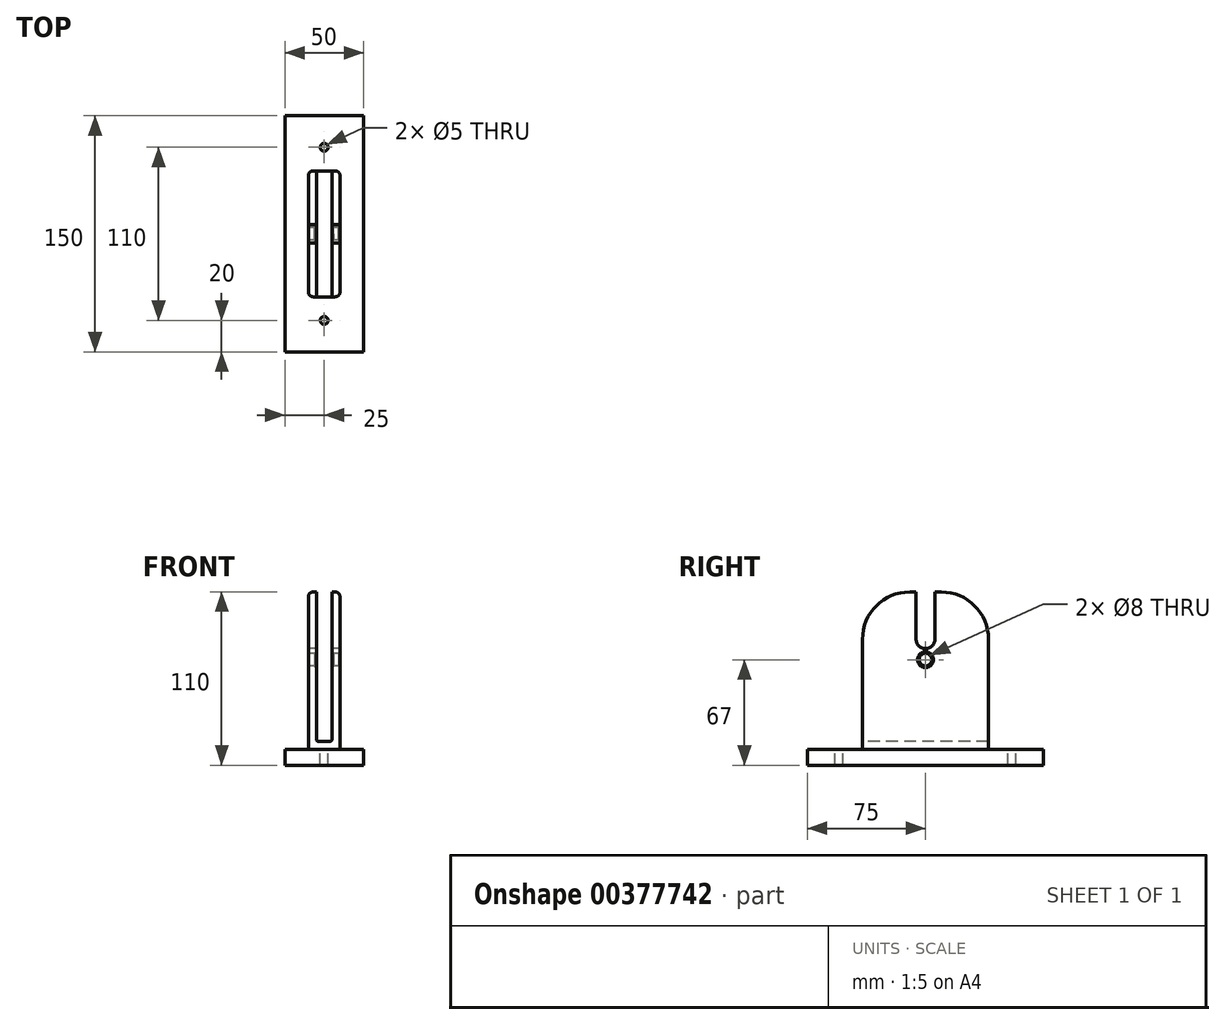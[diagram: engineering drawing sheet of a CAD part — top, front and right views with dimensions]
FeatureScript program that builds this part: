
annotation { "Feature Type Name" : "Feature", "Feature Type Description" : "" }
export const myFeature = defineFeature(function(context is Context, id is Id, definition is map)
    precondition{}
    {
        {
            var Q0;
            Q0=qCreatedBy(makeId("Top.planeOp"),FACE);
            var sketch = newSketch(context, id + "F0", { "sketchPlane" : qUnion([Q0])});
            skLineSegment(sketch, "E0.bottom", {"start": v(25, -75) * mm, "end": v(-25, -75) * mm});
            skLineSegment(sketch, "E0.top", {"start": v(25, 75) * mm, "end": v(-25, 75) * mm});
            skLineSegment(sketch, "E0.left", {"start": v(25, -75) * mm, "end": v(25, 75) * mm});
            skLineSegment(sketch, "E0.right", {"start": v(-25, -75) * mm, "end": v(-25, 75) * mm});
            skPoint(sketch, "E0.middle", {"position": v(0, 0) * mm});
            skLineSegment(sketch, "E1", {"start": v(0, 55) * mm, "end": v(0, -55) * mm, "construction": true});
            skCircle(sketch, "E2", {"center": v(0, 55) * mm, "radius": 2.5 * mm});
            skLineSegment(sketch, "E3", {"start": v(-25, 0) * mm, "end": v(25, 0) * mm, "construction": true});
            skCircle(sketch, "E4.MirrorC", {"center": v(0, -55) * mm, "radius": 2.5 * mm});
            skLineSegment(sketch, "E5.bottom", {"start": v(10, -40) * mm, "end": v(-10, -40) * mm});
            skLineSegment(sketch, "E5.top", {"start": v(10, 40) * mm, "end": v(-10, 40) * mm});
            skLineSegment(sketch, "E5.left", {"start": v(10, -40) * mm, "end": v(10, 40) * mm});
            skLineSegment(sketch, "E5.right", {"start": v(-10, -40) * mm, "end": v(-10, 40) * mm});
            skSolve(sketch);
        }
        {
            var Q0;
            Q0=makeQuery(id+"F0.imprint","IMPRINT",FACE,{"disambiguationData":[TD([[makeQuery(id+"F0.imprint","IMPRINT",EDGE,{"derivedFrom":sQuery(id+"F0.wireOp",EDGE,"E0.bottom")}),-1.0]])]});
            var Q1;
            Q1=makeQuery(id+"F0.imprint","IMPRINT",FACE,{"disambiguationData":[TD([[makeQuery(id+"F0.imprint","IMPRINT",EDGE,{"derivedFrom":sQuery(id+"F0.wireOp",EDGE,"E5.bottom")}),-1.0]])]});
            extrude(context, id + "F1", {"entities" : qUnion([Q0, Q1]), "oppositeDirection" : true, "depth" : 10 * mm});
        }
        {
            var Q0;
            Q0=makeQuery(id+"F0.imprint","IMPRINT",FACE,{"disambiguationData":[TD([[makeQuery(id+"F0.imprint","IMPRINT",EDGE,{"derivedFrom":sQuery(id+"F0.wireOp",EDGE,"E5.bottom")}),-1.0]])]});
            extrude(context, id + "F2", {"entities" : qUnion([Q0]), "operationType" : NewBodyOperationType.ADD, "depth" : 100 * mm});
        }
        {
            var Q0;
            Q0=makeQuery(id+"F2.opExtrude","SWEPT_FACE",FACE,{"disambiguationData":[OSD([sQuery(id+"F0.wireOp",EDGE,"E5.right")])]});
            var sketch = newSketch(context, id + "F3", { "sketchPlane" : qUnion([Q0])});
            skLineSegment(sketch, "E6", {"start": v(0, 100) * mm, "end": v(0, 0) * mm, "construction": true});
            skLineSegment(sketch, "E7", {"start": v(-40, 50) * mm, "end": v(40, 50) * mm, "construction": true});
            skLineSegment(sketch, "E8", {"start": v(-6, 100) * mm, "end": v(-6, 0) * mm, "construction": true});
            skLineSegment(sketch, "E9.MirrorCS", {"start": v(6, 100) * mm, "end": v(6, 0) * mm, "construction": true});
            skLineSegment(sketch, "E10", {"start": v(-40, 70) * mm, "end": v(40, 70) * mm, "construction": true});
            skLineSegment(sketch, "E11", {"start": v(-6, 70) * mm, "end": v(-6, 100) * mm});
            skLineSegment(sketch, "E12", {"start": v(6, 70) * mm, "end": v(6, 100) * mm});
            skArc(sketch, "E13", {"start": v(-6, 70) * mm, "mid": v(0, 64) * mm, "end": v(6, 70) * mm});
            skSolve(sketch);
        }
        {
            var Q0;
            {var subQ0=sQuery(id+"F3.wireOp",EDGE,"E11");Q0=makeQuery(id+"F3.imprint","IMPRINT",FACE,{"disambiguationData":[TD([[makeQuery(id+"F3.imprint","IMPRINT",EDGE,{"derivedFrom":subQ0}),-1.0]])]});}
            extrude(context, id + "F4", {"entities" : qUnion([Q0]), "operationType" : NewBodyOperationType.REMOVE, "endBound" : BoundingType.UP_TO_NEXT, "oppositeDirection" : true, "depth" : 25 * mm});
        }
        {
            var Q0;
            Q0=makeQuery(id+"F2.opExtrude","SWEPT_FACE",FACE,{"disambiguationData":[OSD([sQuery(id+"F0.wireOp",EDGE,"E5.bottom")])]});
            var sketch = newSketch(context, id + "F5", { "sketchPlane" : qUnion([Q0])});
            skLineSegment(sketch, "E14", {"start": v(0, 100) * mm, "end": v(0, 0) * mm, "construction": true});
            skLineSegment(sketch, "E15", {"start": v(-10, 5) * mm, "end": v(10, 5) * mm, "construction": true});
            skLineSegment(sketch, "E16", {"start": v(-5, 100) * mm, "end": v(-5, 0) * mm, "construction": true});
            skLineSegment(sketch, "E17.MirrorCS", {"start": v(5, 100) * mm, "end": v(5, 0) * mm, "construction": true});
            skLineSegment(sketch, "E18", {"start": v(-5, 100) * mm, "end": v(-5, 5) * mm});
            skLineSegment(sketch, "E19", {"start": v(-5, 5) * mm, "end": v(5, 5) * mm});
            skLineSegment(sketch, "E20", {"start": v(5, 5) * mm, "end": v(5, 100) * mm});
            skSolve(sketch);
        }
        {
            var Q0;
            {var subQ0=sQuery(id+"F5.wireOp",EDGE,"E18");Q0=makeQuery(id+"F5.imprint","IMPRINT",FACE,{"disambiguationData":[TD([[makeQuery(id+"F5.imprint","IMPRINT",EDGE,{"derivedFrom":subQ0}),1.0]])]});}
            extrude(context, id + "F6", {"entities" : qUnion([Q0]), "operationType" : NewBodyOperationType.REMOVE, "endBound" : BoundingType.THROUGH_ALL, "oppositeDirection" : true, "depth" : 25 * mm});
        }
        {
            var Q0;
            {var subQ0=sQuery(id+"F5.wireOp",EDGE,"E19");var subQ1=sQuery(id+"F5.wireOp",EDGE,"E20");Q0=makeQuery(id+"F6.boolean.opBoolean","COPY",EDGE,{"disambiguationData":[TD([makeQuery(id+"F2.opExtrude","SWEPT_FACE",FACE,{"disambiguationData":[OSD([sQuery(id+"F0.wireOp",EDGE,"E5.top")])]})])],"derivedFrom":makeQuery(id+"F6.opExtrude","SWEPT_EDGE",EDGE,{"disambiguationData":[OSD([subQ0,subQ1])]})});}
            var Q1;
            {var subQ0=sQuery(id+"F5.wireOp",EDGE,"E19");var subQ1=sQuery(id+"F5.wireOp",EDGE,"E20");Q1=makeQuery(id+"F6.boolean.opBoolean","COPY",EDGE,{"disambiguationData":[TD([makeQuery(id+"F2.opExtrude","SWEPT_FACE",FACE,{"disambiguationData":[OSD([sQuery(id+"F0.wireOp",EDGE,"E5.bottom")])]})])],"derivedFrom":makeQuery(id+"F6.opExtrude","SWEPT_EDGE",EDGE,{"disambiguationData":[OSD([subQ0,subQ1])]})});}
            var Q2;
            {var subQ0=sQuery(id+"F5.wireOp",EDGE,"E18");var subQ1=sQuery(id+"F5.wireOp",EDGE,"E19");Q2=makeQuery(id+"F6.boolean.opBoolean","COPY",EDGE,{"disambiguationData":[TD([makeQuery(id+"F2.opExtrude","SWEPT_FACE",FACE,{"disambiguationData":[OSD([sQuery(id+"F0.wireOp",EDGE,"E5.top")])]})])],"derivedFrom":makeQuery(id+"F6.opExtrude","SWEPT_EDGE",EDGE,{"disambiguationData":[OSD([subQ0,subQ1])]})});}
            var Q3;
            {var subQ0=sQuery(id+"F5.wireOp",EDGE,"E18");var subQ1=sQuery(id+"F5.wireOp",EDGE,"E19");Q3=makeQuery(id+"F6.boolean.opBoolean","COPY",EDGE,{"disambiguationData":[TD([makeQuery(id+"F2.opExtrude","SWEPT_FACE",FACE,{"disambiguationData":[OSD([sQuery(id+"F0.wireOp",EDGE,"E5.bottom")])]})])],"derivedFrom":makeQuery(id+"F6.opExtrude","SWEPT_EDGE",EDGE,{"disambiguationData":[OSD([subQ0,subQ1])]})});}
            fillet(context, id + "F7", {"entities" : qUnion([Q0, Q1, Q2, Q3]), "radius" : 1.5 * mm, "tangentPropagation" : true, "allowEdgeOverflow" : false});
        }
        {
            var Q0;
            Q0=makeQuery(id+"F2.opExtrude","SWEPT_FACE",FACE,{"disambiguationData":[OSD([sQuery(id+"F0.wireOp",EDGE,"E5.right")])]});
            var sketch = newSketch(context, id + "F8", { "sketchPlane" : qUnion([Q0])});
            skLineSegment(sketch, "E21", {"start": v(0, 0) * mm, "end": v(0, 64) * mm, "construction": true});
            skLineSegment(sketch, "E22", {"start": v(-40, 57) * mm, "end": v(40, 57) * mm, "construction": true});
            skCircle(sketch, "E23", {"center": v(0, 57) * mm, "radius": 4 * mm});
            skSolve(sketch);
        }
        {
            var Q0;
            Q0=makeQuery(id+"F8.imprint","IMPRINT",FACE,{"disambiguationData":[TD([[makeQuery(id+"F8.imprint","IMPRINT",EDGE,{"derivedFrom":sQuery(id+"F8.wireOp",EDGE,"E23")}),1.0]])]});
            extrude(context, id + "F9", {"entities" : qUnion([Q0]), "operationType" : NewBodyOperationType.REMOVE, "endBound" : BoundingType.THROUGH_ALL, "oppositeDirection" : true, "depth" : 25 * mm});
        }
        {
            var Q0;
            Q0=makeQuery(id+"F9.boolean.opBoolean","COPY",EDGE,{"derivedFrom":makeQuery(id+"F9.opExtrude","CAP_EDGE",EDGE,{"disambiguationData":[OSD([sQuery(id+"F8.wireOp",EDGE,"E23")])],"isStart":true})});
            var Q1;
            Q1=makeQuery(id+"F9.boolean.opBoolean","INTERSECT",EDGE,{"derivedFrom":[makeQuery(id+"F6.boolean.opBoolean","COPY",FACE,{"derivedFrom":makeQuery(id+"F6.opExtrude","SWEPT_FACE",FACE,{"disambiguationData":[OSD([sQuery(id+"F5.wireOp",EDGE,"E18")])]})}),makeQuery(id+"F9.opExtrude","SWEPT_FACE",FACE,{"disambiguationData":[OSD([sQuery(id+"F8.wireOp",EDGE,"E23")])]})]});
            var Q2;
            Q2=makeQuery(id+"F9.boolean.opBoolean","INTERSECT",EDGE,{"derivedFrom":[makeQuery(id+"F6.boolean.opBoolean","COPY",FACE,{"derivedFrom":makeQuery(id+"F6.opExtrude","SWEPT_FACE",FACE,{"disambiguationData":[OSD([sQuery(id+"F5.wireOp",EDGE,"E20")])]})}),makeQuery(id+"F9.opExtrude","SWEPT_FACE",FACE,{"disambiguationData":[OSD([sQuery(id+"F8.wireOp",EDGE,"E23")])]})]});
            var Q3;
            Q3=makeQuery(id+"F9.boolean.opBoolean","INTERSECT",EDGE,{"derivedFrom":[makeQuery(id+"F2.opExtrude","SWEPT_FACE",FACE,{"disambiguationData":[OSD([sQuery(id+"F0.wireOp",EDGE,"E5.left")])]}),makeQuery(id+"F9.opExtrude","SWEPT_FACE",FACE,{"disambiguationData":[OSD([sQuery(id+"F8.wireOp",EDGE,"E23")])]})]});
            chamfer(context, id + "F10", {"entities" : qUnion([Q0, Q1, Q2, Q3]), "width" : 1 * mm, "tangentPropagation" : true});
        }
        {
            var Q0;
            {var subQ0=sQuery(id+"F0.wireOp",EDGE,"E5.right");var subQ1=sQuery(id+"F0.wireOp",EDGE,"E5.top");Q0=makeQuery(id+"F6.boolean.opBoolean","SPLIT",EDGE,{"disambiguationData":[TD([makeQuery(id+"F2.opExtrude","SWEPT_FACE",FACE,{"disambiguationData":[OSD([subQ0])]})])],"derivedFrom":makeQuery(id+"F2.opExtrude","CAP_EDGE",EDGE,{"disambiguationData":[OSD([subQ1])],"isStart":false})});}
            var Q1;
            {var subQ0=sQuery(id+"F0.wireOp",EDGE,"E5.left");var subQ1=sQuery(id+"F0.wireOp",EDGE,"E5.top");Q1=makeQuery(id+"F6.boolean.opBoolean","SPLIT",EDGE,{"disambiguationData":[TD([makeQuery(id+"F2.opExtrude","SWEPT_FACE",FACE,{"disambiguationData":[OSD([subQ0])]})])],"derivedFrom":makeQuery(id+"F2.opExtrude","CAP_EDGE",EDGE,{"disambiguationData":[OSD([subQ1])],"isStart":false})});}
            var Q2;
            {var subQ0=sQuery(id+"F0.wireOp",EDGE,"E5.bottom");var subQ1=sQuery(id+"F0.wireOp",EDGE,"E5.left");Q2=makeQuery(id+"F6.boolean.opBoolean","SPLIT",EDGE,{"disambiguationData":[TD([makeQuery(id+"F2.opExtrude","SWEPT_FACE",FACE,{"disambiguationData":[OSD([subQ1])]})])],"derivedFrom":makeQuery(id+"F2.opExtrude","CAP_EDGE",EDGE,{"disambiguationData":[OSD([subQ0])],"isStart":false})});}
            var Q3;
            {var subQ0=sQuery(id+"F0.wireOp",EDGE,"E5.bottom");var subQ1=sQuery(id+"F0.wireOp",EDGE,"E5.right");Q3=makeQuery(id+"F6.boolean.opBoolean","SPLIT",EDGE,{"disambiguationData":[TD([makeQuery(id+"F2.opExtrude","SWEPT_FACE",FACE,{"disambiguationData":[OSD([subQ1])]})])],"derivedFrom":makeQuery(id+"F2.opExtrude","CAP_EDGE",EDGE,{"disambiguationData":[OSD([subQ0])],"isStart":false})});}
            fillet(context, id + "F11", {"entities" : qUnion([Q0, Q1, Q2, Q3]), "radius" : 30 * mm, "tangentPropagation" : true, "allowEdgeOverflow" : false});
        }
        {
            var Q0;
            {var subQ0=sQuery(id+"F0.wireOp",EDGE,"E5.right");var subQ1=makeQuery(id+"F2.opExtrude","SWEPT_FACE",FACE,{"disambiguationData":[OSD([subQ0])]});var subQ2=sQuery(id+"F0.wireOp",EDGE,"E5.top");Q0=makeQuery(id+"F11.opFillet","BLEND_EDGE",EDGE,{"blendedFrom":[makeQuery(id+"F6.boolean.opBoolean","SPLIT",EDGE,{"disambiguationData":[TD([subQ1])],"derivedFrom":makeQuery(id+"F2.opExtrude","CAP_EDGE",EDGE,{"disambiguationData":[OSD([subQ2])],"isStart":false})}),subQ1],"blendedInto":[subQ1]});}
            var Q1;
            {var subQ0=sQuery(id+"F0.wireOp",EDGE,"E5.right");var subQ1=sQuery(id+"F0.wireOp",EDGE,"E5.top");Q1=makeQuery(id+"F4.boolean.opBoolean","SPLIT",EDGE,{"disambiguationData":[TD([makeQuery(id+"F2.opExtrude","SWEPT_FACE",FACE,{"disambiguationData":[OSD([subQ1])]})])],"derivedFrom":makeQuery(id+"F2.opExtrude","CAP_EDGE",EDGE,{"disambiguationData":[OSD([subQ0])],"isStart":false})});}
            var Q2;
            {var subQ0=sQuery(id+"F0.wireOp",EDGE,"E5.bottom");var subQ1=sQuery(id+"F0.wireOp",EDGE,"E5.right");Q2=makeQuery(id+"F4.boolean.opBoolean","SPLIT",EDGE,{"disambiguationData":[TD([makeQuery(id+"F2.opExtrude","SWEPT_FACE",FACE,{"disambiguationData":[OSD([subQ0])]})])],"derivedFrom":makeQuery(id+"F2.opExtrude","CAP_EDGE",EDGE,{"disambiguationData":[OSD([subQ1])],"isStart":false})});}
            var Q3;
            {var subQ0=sQuery(id+"F0.wireOp",EDGE,"E5.right");var subQ1=makeQuery(id+"F2.opExtrude","SWEPT_FACE",FACE,{"disambiguationData":[OSD([subQ0])]});var subQ2=sQuery(id+"F0.wireOp",EDGE,"E5.bottom");Q3=makeQuery(id+"F11.opFillet","BLEND_EDGE",EDGE,{"blendedFrom":[makeQuery(id+"F6.boolean.opBoolean","SPLIT",EDGE,{"disambiguationData":[TD([subQ1])],"derivedFrom":makeQuery(id+"F2.opExtrude","CAP_EDGE",EDGE,{"disambiguationData":[OSD([subQ2])],"isStart":false})}),subQ1],"blendedInto":[subQ1]});}
            var Q4;
            {var subQ0=sQuery(id+"F0.wireOp",EDGE,"E5.left");var subQ1=makeQuery(id+"F2.opExtrude","SWEPT_FACE",FACE,{"disambiguationData":[OSD([subQ0])]});var subQ2=sQuery(id+"F0.wireOp",EDGE,"E5.bottom");Q4=makeQuery(id+"F11.opFillet","BLEND_EDGE",EDGE,{"blendedFrom":[makeQuery(id+"F6.boolean.opBoolean","SPLIT",EDGE,{"disambiguationData":[TD([subQ1])],"derivedFrom":makeQuery(id+"F2.opExtrude","CAP_EDGE",EDGE,{"disambiguationData":[OSD([subQ2])],"isStart":false})}),subQ1],"blendedInto":[subQ1]});}
            var Q5;
            {var subQ0=sQuery(id+"F0.wireOp",EDGE,"E5.bottom");var subQ1=sQuery(id+"F0.wireOp",EDGE,"E5.left");Q5=makeQuery(id+"F4.boolean.opBoolean","SPLIT",EDGE,{"disambiguationData":[TD([makeQuery(id+"F2.opExtrude","SWEPT_FACE",FACE,{"disambiguationData":[OSD([subQ0])]})])],"derivedFrom":makeQuery(id+"F2.opExtrude","CAP_EDGE",EDGE,{"disambiguationData":[OSD([subQ1])],"isStart":false})});}
            var Q6;
            {var subQ0=sQuery(id+"F0.wireOp",EDGE,"E5.left");var subQ1=sQuery(id+"F0.wireOp",EDGE,"E5.top");Q6=makeQuery(id+"F4.boolean.opBoolean","SPLIT",EDGE,{"disambiguationData":[TD([makeQuery(id+"F2.opExtrude","SWEPT_FACE",FACE,{"disambiguationData":[OSD([subQ1])]})])],"derivedFrom":makeQuery(id+"F2.opExtrude","CAP_EDGE",EDGE,{"disambiguationData":[OSD([subQ0])],"isStart":false})});}
            var Q7;
            {var subQ0=sQuery(id+"F0.wireOp",EDGE,"E5.left");var subQ1=makeQuery(id+"F2.opExtrude","SWEPT_FACE",FACE,{"disambiguationData":[OSD([subQ0])]});var subQ2=sQuery(id+"F0.wireOp",EDGE,"E5.top");Q7=makeQuery(id+"F11.opFillet","BLEND_EDGE",EDGE,{"blendedFrom":[makeQuery(id+"F6.boolean.opBoolean","SPLIT",EDGE,{"disambiguationData":[TD([subQ1])],"derivedFrom":makeQuery(id+"F2.opExtrude","CAP_EDGE",EDGE,{"disambiguationData":[OSD([subQ2])],"isStart":false})}),subQ1],"blendedInto":[subQ1]});}
            fillet(context, id + "F12", {"entities" : qUnion([Q0, Q1, Q2, Q3, Q4, Q5, Q6, Q7]), "radius" : 3 * mm, "tangentPropagation" : true, "allowEdgeOverflow" : false});
        }
    });
